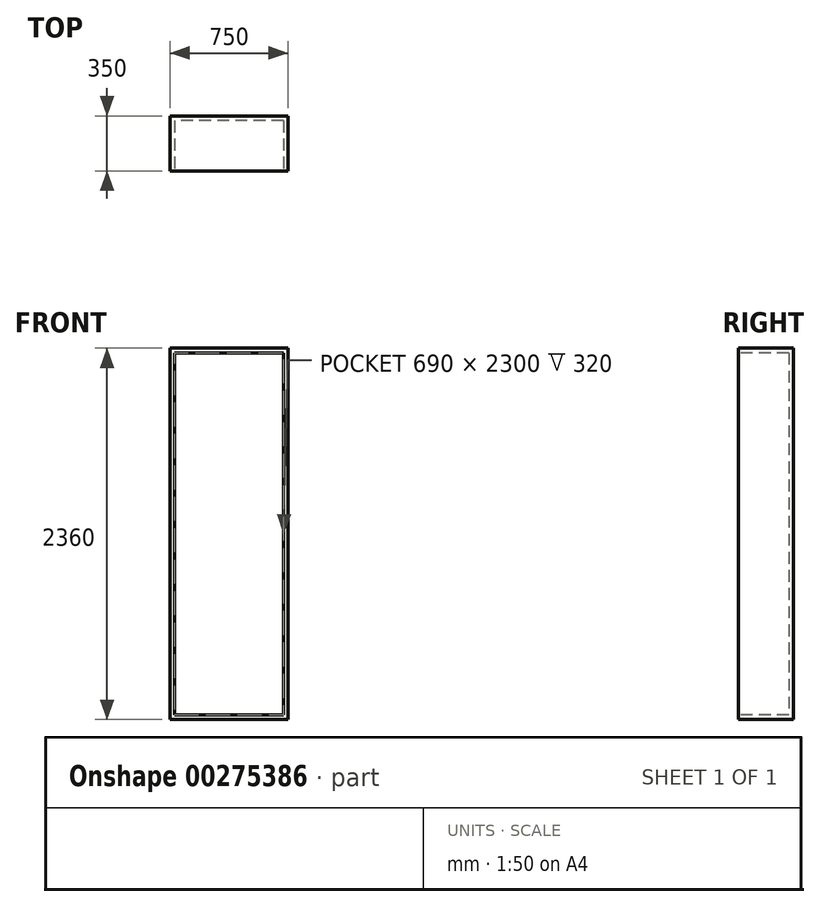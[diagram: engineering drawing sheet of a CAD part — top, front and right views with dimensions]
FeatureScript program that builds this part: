
annotation { "Feature Type Name" : "Feature", "Feature Type Description" : "" }
export const myFeature = defineFeature(function(context is Context, id is Id, definition is map)
    precondition{}
    {
        {
            var Q0;
            Q0=qCreatedBy(makeId("Top.planeOp"),FACE);
            var sketch = newSketch(context, id + "F0", { "sketchPlane" : qUnion([Q0])});
            skLineSegment(sketch, "E0.bottom", {"start": v(375, 175) * mm, "end": v(-375, 175) * mm});
            skLineSegment(sketch, "E0.top", {"start": v(375, -175) * mm, "end": v(-375, -175) * mm});
            skLineSegment(sketch, "E0.left", {"start": v(375, 175) * mm, "end": v(375, -175) * mm});
            skLineSegment(sketch, "E0.right", {"start": v(-375, 175) * mm, "end": v(-375, -175) * mm});
            skPoint(sketch, "E0.middle", {"position": v(0, 0) * mm});
            skSolve(sketch);
        }
        {
            var Q0;
            Q0=qSketchRegion(id+"F0",true);
            extrude(context, id + "F1", {"entities" : qUnion([Q0]), "depth" : 2360 * mm});
        }
        {
            var Q0;
            Q0=makeQuery(id+"F1.opExtrude","SWEPT_FACE",FACE,{"disambiguationData":[OSD([sQuery(id+"F0.wireOp",EDGE,"E0.top")])]});
            shell(context, id + "F2", {"entities" : qUnion([Q0]), "thickness" : 30 * mm});
        }
    });
